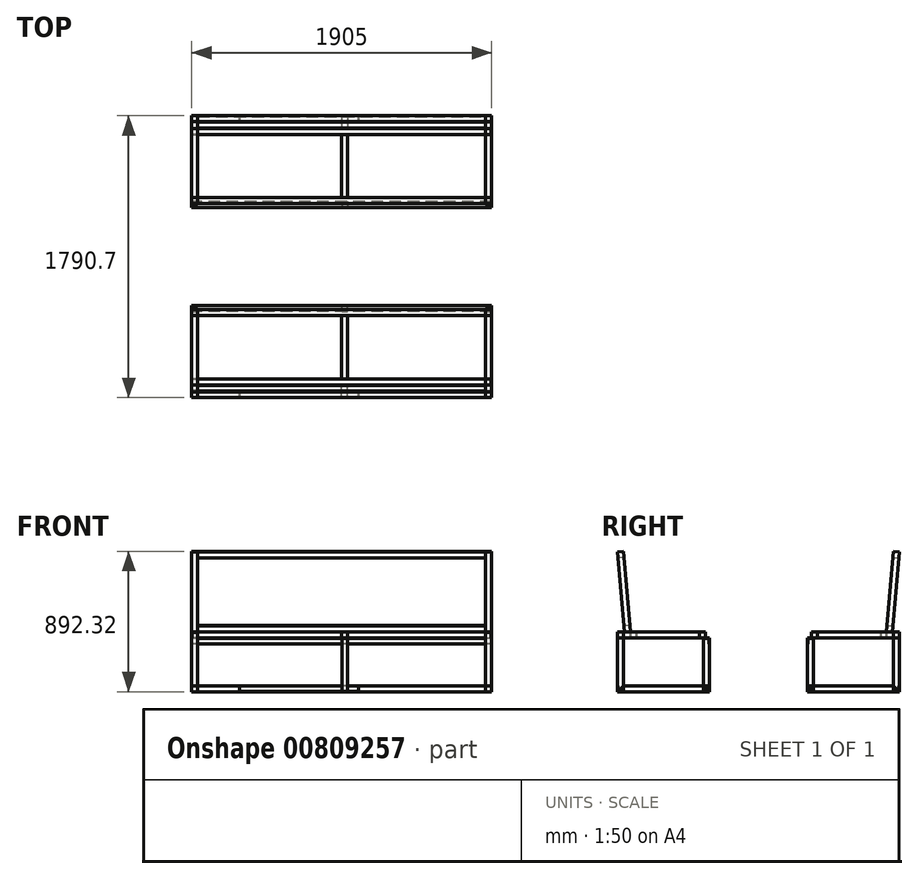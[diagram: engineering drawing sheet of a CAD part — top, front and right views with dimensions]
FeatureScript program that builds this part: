
annotation { "Feature Type Name" : "Feature", "Feature Type Description" : "" }
export const myFeature = defineFeature(function(context is Context, id is Id, definition is map)
    precondition{}
    {
        {
            var Q0;
            Q0=qCreatedBy(makeId("Front.planeOp"),FACE);
            var sketch = newSketch(context, id + "F0", { "sketchPlane" : qUnion([Q0])});
            skLineSegment(sketch, "E0", {"start": v(0, 0) * mm, "end": v(0, 38.1) * mm});
            skLineSegment(sketch, "E1", {"start": v(0, 0) * mm, "end": v(38.1, 0) * mm});
            skLineSegment(sketch, "E2", {"start": v(0, 38.1) * mm, "end": v(3.17, 38.1) * mm});
            skLineSegment(sketch, "E3", {"start": v(3.17, 38.1) * mm, "end": v(3.18, 3.17) * mm});
            skLineSegment(sketch, "E4", {"start": v(3.18, 3.17) * mm, "end": v(38.1, 3.17) * mm});
            skLineSegment(sketch, "E5", {"start": v(38.1, 3.17) * mm, "end": v(38.1, 0) * mm});
            skSolve(sketch);
        }
        {
            var Q0;
            Q0 = qSketchRegion(id + "F0", true);
            extrude(context, id + "F1", {"entities" : qUnion([Q0]), "endBound" : BoundingType.SYMMETRIC, "depth" : 584.2 * mm, "offsetDistance" : 25.4 * mm});
        }
        {
            var Q0;
            Q0=makeQuery(id+"F1.opExtrude","SWEPT_EDGE",EDGE,{"disambiguationData":[OSD([sQuery(id+"F0.wireOp",EDGE,"E2"),sQuery(id+"F0.wireOp",EDGE,"E3")])]});
            var Q1;
            Q1=makeQuery(id+"F1.opExtrude","SWEPT_EDGE",EDGE,{"disambiguationData":[OSD([sQuery(id+"F0.wireOp",EDGE,"E3"),sQuery(id+"F0.wireOp",EDGE,"E4")])]});
            var Q2;
            Q2=makeQuery(id+"F1.opExtrude","SWEPT_EDGE",EDGE,{"disambiguationData":[OSD([sQuery(id+"F0.wireOp",EDGE,"E4"),sQuery(id+"F0.wireOp",EDGE,"E5")])]});
            fillet(context, id + "F2", {"entities" : qUnion([Q0, Q1, Q2]), "radius" : 3.17 * mm, "tangentPropagation" : true, "allowEdgeOverflow" : false});
        }
        {
            var Q0;
            Q0=makeQuery(id+"F1.opExtrude","SWEPT_FACE",FACE,{"disambiguationData":[OSD([sQuery(id+"F0.wireOp",EDGE,"E0")])]});
            var sketch = newSketch(context, id + "F3", { "sketchPlane" : qUnion([Q0])});
            skLineSegment(sketch, "E6", {"start": v(-292.1, 0) * mm, "end": v(-254, 38.1) * mm});
            skSolve(sketch);
        }
        {
            var Q0;
            Q0 = qSketchRegion(id + "F3", true);
            var Q1;
            {var subQ0=sQuery(id+"F3.wireOp",EDGE,"E6");Q1=makeQuery(id+"F3.imprint","IMPRINT",FACE,{"disambiguationData":[TD([[makeQuery(id+"F3.imprint","IMPRINT",EDGE,{"derivedFrom":subQ0}),1.0]])]});}
            extrude(context, id + "F4", {"entities" : qUnion([Q0, Q1]), "operationType" : NewBodyOperationType.REMOVE, "endBound" : BoundingType.THROUGH_ALL, "oppositeDirection" : true, "depth" : 25.4 * mm, "offsetDistance" : 25.4 * mm});
        }
        {
            var Q0;
            Q0=qCreatedBy(makeId("Top.planeOp"),FACE);
            cPlane(context, id + "F5", {"entities" : qUnion([Q0]), "cplaneType" : CPlaneType.OFFSET, "offset" : 190.5 * mm, "width" : 152.4 * mm, "height" : 152.4 * mm});
        }
        {
            var Q0;
            Q0=qCreatedBy(id+"F5.planeOp",FACE);
            var sketch = newSketch(context, id + "F6", { "sketchPlane" : qUnion([Q0])});
            skLineSegment(sketch, "E7", {"start": v(38.1, 292.1) * mm, "end": v(0, 292.1) * mm});
            skLineSegment(sketch, "E8", {"start": v(0, 292.1) * mm, "end": v(0, 254) * mm});
            skLineSegment(sketch, "E9", {"start": v(38.1, 292.1) * mm, "end": v(38.1, 288.93) * mm});
            skLineSegment(sketch, "E10", {"start": v(38.1, 288.93) * mm, "end": v(3.17, 288.93) * mm});
            skLineSegment(sketch, "E11", {"start": v(3.17, 288.93) * mm, "end": v(3.17, 254) * mm});
            skLineSegment(sketch, "E12", {"start": v(3.17, 254) * mm, "end": v(0, 254) * mm});
            skSolve(sketch);
        }
        {
            var Q0;
            Q0 = qSketchRegion(id + "F6", true);
            extrude(context, id + "F7", {"entities" : qUnion([Q0]), "endBound" : BoundingType.SYMMETRIC, "depth" : 381 * mm, "offsetDistance" : 25.4 * mm});
        }
        {
            var Q0;
            Q0=makeQuery(id+"F7.opExtrude","SWEPT_EDGE",EDGE,{"disambiguationData":[OSD([sQuery(id+"F6.wireOp",EDGE,"E9"),sQuery(id+"F6.wireOp",EDGE,"E10")])]});
            var Q1;
            Q1=makeQuery(id+"F7.opExtrude","SWEPT_EDGE",EDGE,{"disambiguationData":[OSD([sQuery(id+"F6.wireOp",EDGE,"E10"),sQuery(id+"F6.wireOp",EDGE,"E11")])]});
            var Q2;
            Q2=makeQuery(id+"F7.opExtrude","SWEPT_EDGE",EDGE,{"disambiguationData":[OSD([sQuery(id+"F6.wireOp",EDGE,"E11"),sQuery(id+"F6.wireOp",EDGE,"E12")])]});
            fillet(context, id + "F8", {"entities" : qUnion([Q0, Q1, Q2]), "radius" : 3.17 * mm, "allowEdgeOverflow" : false});
        }
        {
            var Q0;
            Q0=makeQuery(id+"F7.opExtrude","SWEPT_FACE",FACE,{"disambiguationData":[OSD([sQuery(id+"F6.wireOp",EDGE,"E8")])]});
            var sketch = newSketch(context, id + "F9", { "sketchPlane" : qUnion([Q0])});
            skLineSegment(sketch, "E13", {"start": v(-292.1, 0) * mm, "end": v(-254, 38.1) * mm});
            skLineSegment(sketch, "E14", {"start": v(-254, 38.1) * mm, "end": v(-254, 0) * mm});
            skLineSegment(sketch, "E15", {"start": v(-254, 0) * mm, "end": v(-292.1, 0) * mm});
            skSolve(sketch);
        }
        {
            var Q0;
            Q0 = qSketchRegion(id + "F9", true);
            extrude(context, id + "F10", {"entities" : qUnion([Q0]), "operationType" : NewBodyOperationType.REMOVE, "endBound" : BoundingType.THROUGH_ALL, "oppositeDirection" : true, "depth" : 25.4 * mm, "offsetDistance" : 25.4 * mm});
        }
        {
            var Q0;
            Q0=qCreatedBy(id+"F5.planeOp",FACE);
            var sketch = newSketch(context, id + "F11", { "sketchPlane" : qUnion([Q0])});
            skLineSegment(sketch, "E16", {"start": v(38.1, -292.1) * mm, "end": v(0, -292.1) * mm});
            skLineSegment(sketch, "E17", {"start": v(0, -292.1) * mm, "end": v(0, -254) * mm});
            skLineSegment(sketch, "E18", {"start": v(0, -254) * mm, "end": v(3.18, -254) * mm});
            skLineSegment(sketch, "E19", {"start": v(3.18, -254) * mm, "end": v(3.18, -288.93) * mm});
            skLineSegment(sketch, "E20", {"start": v(3.18, -288.93) * mm, "end": v(38.1, -288.93) * mm});
            skLineSegment(sketch, "E21", {"start": v(38.1, -288.93) * mm, "end": v(38.1, -292.1) * mm});
            skSolve(sketch);
        }
        {
            var Q0;
            Q0 = qSketchRegion(id + "F11", true);
            var Q1;
            Q1=makeQuery(id+"F1.opExtrude","SWEPT_FACE",FACE,{"disambiguationData":[OSD([sQuery(id+"F0.wireOp",EDGE,"E1")])]});
            extrude(context, id + "F12", {"entities" : qUnion([Q0]), "endBound" : BoundingType.UP_TO_SURFACE, "oppositeDirection" : true, "depth" : 25.4 * mm, "endBoundEntityFace" : qUnion([Q1]), "offsetDistance" : 25.4 * mm, "hasSecondDirection" : true, "secondDirectionOppositeDirection" : false, "secondDirectionDepth" : 152.4 * mm});
        }
        {
            var Q0;
            Q0=makeQuery(id+"F12.opExtrude","SWEPT_FACE",FACE,{"disambiguationData":[OSD([sQuery(id+"F11.wireOp",EDGE,"E17")])]});
            var sketch = newSketch(context, id + "F13", { "sketchPlane" : qUnion([Q0])});
            skLineSegment(sketch, "E22", {"start": v(292.1, 342.9) * mm, "end": v(254, 304.8) * mm});
            skLineSegment(sketch, "E23", {"start": v(254, 304.8) * mm, "end": v(254, 342.9) * mm});
            skLineSegment(sketch, "E24", {"start": v(254, 342.9) * mm, "end": v(292.1, 342.9) * mm});
            skSolve(sketch);
        }
        {
            var Q0;
            Q0=makeQuery(id+"F12.opExtrude","SWEPT_FACE",FACE,{"disambiguationData":[OSD([sQuery(id+"F11.wireOp",EDGE,"E17")])]});
            var sketch = newSketch(context, id + "F14", { "sketchPlane" : qUnion([Q0])});
            skLineSegment(sketch, "E25", {"start": v(292.1, 0) * mm, "end": v(254, 38.1) * mm});
            skLineSegment(sketch, "E26", {"start": v(254, 38.1) * mm, "end": v(254, 0) * mm});
            skLineSegment(sketch, "E27", {"start": v(254, 0) * mm, "end": v(292.1, 0) * mm});
            skSolve(sketch);
        }
        {
            var Q0;
            Q0 = qSketchRegion(id + "F14", true);
            extrude(context, id + "F15", {"entities" : qUnion([Q0]), "operationType" : NewBodyOperationType.REMOVE, "endBound" : BoundingType.THROUGH_ALL, "oppositeDirection" : true, "depth" : 25.4 * mm, "offsetDistance" : 25.4 * mm});
        }
        {
            var Q0;
            Q0=makeQuery(id+"F7.opExtrude","SWEPT_FACE",FACE,{"disambiguationData":[OSD([sQuery(id+"F6.wireOp",EDGE,"E7")])]});
            var sketch = newSketch(context, id + "F16", { "sketchPlane" : qUnion([Q0])});
            skLineSegment(sketch, "E28", {"start": v(-38.1, 381) * mm, "end": v(0, 381) * mm});
            skLineSegment(sketch, "E29", {"start": v(0, 381) * mm, "end": v(0, 342.9) * mm});
            skLineSegment(sketch, "E30", {"start": v(-38.1, 381) * mm, "end": v(-38.1, 377.83) * mm});
            skLineSegment(sketch, "E31", {"start": v(-38.1, 377.83) * mm, "end": v(-3.18, 377.83) * mm});
            skLineSegment(sketch, "E32", {"start": v(-3.18, 377.83) * mm, "end": v(-3.18, 342.9) * mm});
            skLineSegment(sketch, "E33", {"start": v(-3.18, 342.9) * mm, "end": v(0, 342.9) * mm});
            skSolve(sketch);
        }
        {
            var Q0;
            Q0 = qSketchRegion(id + "F16", true);
            extrude(context, id + "F17", {"entities" : qUnion([Q0]), "oppositeDirection" : true, "depth" : 558.8 * mm, "offsetDistance" : 25.4 * mm});
        }
        {
            var Q0;
            Q0=makeQuery(id+"F17.opExtrude","SWEPT_FACE",FACE,{"disambiguationData":[OSD([sQuery(id+"F16.wireOp",EDGE,"E29")])]});
            var sketch = newSketch(context, id + "F18", { "sketchPlane" : qUnion([Q0])});
            skLineSegment(sketch, "E34", {"start": v(266.7, 381) * mm, "end": v(228.6, 342.9) * mm});
            skLineSegment(sketch, "E35", {"start": v(228.6, 342.9) * mm, "end": v(266.7, 342.9) * mm});
            skLineSegment(sketch, "E36", {"start": v(266.7, 342.9) * mm, "end": v(266.7, 381) * mm});
            skSolve(sketch);
        }
        {
            var Q0;
            {var subQ0=sQuery(id+"F13.wireOp",EDGE,"E22");Q0=makeQuery(id+"F13.imprint","IMPRINT",FACE,{"disambiguationData":[TD([[makeQuery(id+"F13.imprint","IMPRINT",EDGE,{"derivedFrom":subQ0}),1.0]])]});}
            var sketch = newSketch(context, id + "F19", { "sketchPlane" : qUnion([Q0])});
            skLineSegment(sketch, "E37", {"start": v(254, 0) * mm, "end": v(292.1, 0) * mm});
            skLineSegment(sketch, "E38", {"start": v(292.1, 0) * mm, "end": v(292.1, 38.1) * mm});
            skLineSegment(sketch, "E39", {"start": v(292.1, 38.1) * mm, "end": v(288.93, 38.1) * mm});
            skLineSegment(sketch, "E40", {"start": v(288.93, 38.1) * mm, "end": v(288.93, 3.17) * mm});
            skLineSegment(sketch, "E41", {"start": v(288.93, 3.17) * mm, "end": v(254, 3.17) * mm});
            skLineSegment(sketch, "E42", {"start": v(254, 3.17) * mm, "end": v(254, 0) * mm});
            skSolve(sketch);
        }
        {
            var Q0;
            Q0 = qSketchRegion(id + "F19", true);
            extrude(context, id + "F20", {"entities" : qUnion([Q0]), "oppositeDirection" : true, "depth" : 1905 * mm, "offsetDistance" : 25.4 * mm});
        }
        {
            var Q0;
            {var subQ0=sQuery(id+"F13.wireOp",EDGE,"E22");Q0=makeQuery(id+"F13.imprint","IMPRINT",FACE,{"disambiguationData":[TD([[makeQuery(id+"F13.imprint","IMPRINT",EDGE,{"derivedFrom":subQ0}),1.0]])]});}
            var sketch = newSketch(context, id + "F21", { "sketchPlane" : qUnion([Q0])});
            skLineSegment(sketch, "E43", {"start": v(292.1, 304.8) * mm, "end": v(292.1, 342.9) * mm});
            skLineSegment(sketch, "E44", {"start": v(292.1, 342.9) * mm, "end": v(254, 342.9) * mm});
            skLineSegment(sketch, "E45", {"start": v(254, 342.9) * mm, "end": v(254, 339.73) * mm});
            skLineSegment(sketch, "E46", {"start": v(254, 339.73) * mm, "end": v(288.93, 339.73) * mm});
            skLineSegment(sketch, "E47", {"start": v(288.93, 339.73) * mm, "end": v(288.93, 304.8) * mm});
            skLineSegment(sketch, "E48", {"start": v(288.93, 304.8) * mm, "end": v(292.1, 304.8) * mm});
            skSolve(sketch);
        }
        {
            var Q0;
            Q0 = qSketchRegion(id + "F21", true);
            extrude(context, id + "F22", {"entities" : qUnion([Q0]), "oppositeDirection" : true, "depth" : 1905 * mm, "offsetDistance" : 25.4 * mm});
        }
        {
            var Q0;
            Q0=makeQuery(id+"F18.imprint","IMPRINT",FACE,{"disambiguationData":[TD([[makeQuery(id+"F18.imprint","IMPRINT",EDGE,{"derivedFrom":sQuery(id+"F18.wireOp",EDGE,"E34")}),1.0]])]});
            var sketch = newSketch(context, id + "F23", { "sketchPlane" : qUnion([Q0])});
            skLineSegment(sketch, "E49", {"start": v(228.6, 381) * mm, "end": v(266.7, 381) * mm});
            skLineSegment(sketch, "E50", {"start": v(266.7, 381) * mm, "end": v(266.7, 342.9) * mm});
            skLineSegment(sketch, "E51", {"start": v(266.7, 342.9) * mm, "end": v(228.6, 342.9) * mm});
            skLineSegment(sketch, "E52", {"start": v(228.6, 342.9) * mm, "end": v(228.6, 381) * mm});
            skSolve(sketch);
        }
        {
            var Q0;
            Q0 = qSketchRegion(id + "F23", true);
            extrude(context, id + "F24", {"entities" : qUnion([Q0]), "oppositeDirection" : true, "depth" : 1905 * mm, "offsetDistance" : 25.4 * mm});
        }
        {
            var Q0;
            Q0=makeQuery(id+"F7.opExtrude","SWEPT_FACE",FACE,{"disambiguationData":[OSD([sQuery(id+"F6.wireOp",EDGE,"E8")])]});
            var sketch = newSketch(context, id + "F25", { "sketchPlane" : qUnion([Q0])});
            skLineSegment(sketch, "E53", {"start": v(-292.1, 38.1) * mm, "end": v(-292.1, 0) * mm});
            skLineSegment(sketch, "E54", {"start": v(-292.1, 0) * mm, "end": v(-254, 0) * mm});
            skLineSegment(sketch, "E55", {"start": v(-254, 0) * mm, "end": v(-254, 3.17) * mm});
            skLineSegment(sketch, "E56", {"start": v(-254, 3.17) * mm, "end": v(-288.93, 3.17) * mm});
            skLineSegment(sketch, "E57", {"start": v(-288.93, 3.17) * mm, "end": v(-288.93, 38.1) * mm});
            skLineSegment(sketch, "E58", {"start": v(-288.93, 38.1) * mm, "end": v(-292.1, 38.1) * mm});
            skSolve(sketch);
        }
        {
            var Q0;
            Q0 = qSketchRegion(id + "F25", true);
            extrude(context, id + "F26", {"entities" : qUnion([Q0]), "oppositeDirection" : true, "depth" : 304.8 * mm, "offsetDistance" : 25.4 * mm});
        }
        {
            var Q0;
            Q0=makeQuery(id+"F22.opExtrude","SWEPT_EDGE",EDGE,{"disambiguationData":[OSD([sQuery(id+"F11.wireOp",EDGE,"E16"),sQuery(id+"F11.wireOp",EDGE,"E17"),sQuery(id+"F21.wireOp",EDGE,"E43"),sQuery(id+"F21.wireOp",EDGE,"E48")])]});
            cPoint(context, id + "F27", {"entities" : qUnion([Q0]), "parameter" : 0.5});
        }
        {
            var Q0;
            Q0=makeQuery(id+"F22.opExtrude","SWEPT_EDGE",EDGE,{"disambiguationData":[OSD([sQuery(id+"F13.wireOp",EDGE,"E22"),sQuery(id+"F21.wireOp",EDGE,"E43"),sQuery(id+"F21.wireOp",EDGE,"E44")])]});
            cPoint(context, id + "F28", {"entities" : qUnion([Q0]), "parameter" : 0.5});
        }
        {
            var Q0;
            Q0=makeQuery(id+"F24.opExtrude","SWEPT_EDGE",EDGE,{"disambiguationData":[OSD([sQuery(id+"F18.wireOp",EDGE,"E34"),sQuery(id+"F23.wireOp",EDGE,"E49"),sQuery(id+"F23.wireOp",EDGE,"E50")])]});
            cPoint(context, id + "F29", {"entities" : qUnion([Q0]), "parameter" : 0.5});
        }
        {
            var Q0;
            Q0 = qCreatedBy(id + "F27" ,VERTEX);
            var Q1;
            Q1 = qCreatedBy(id + "F28" ,VERTEX);
            var Q2;
            Q2 = qCreatedBy(id + "F29" ,VERTEX);
            cPlane(context, id + "F30", {"entities" : qUnion([Q0, Q1, Q2]), "cplaneType" : CPlaneType.THREE_POINT, "offset" : 25.4 * mm, "width" : 152.4 * mm, "height" : 152.4 * mm});
        }
        {
            var Q0;
            Q0=makeQuery(id+"F17.opExtrude","SWEPT_BODY",BODY,{"disambiguationData":[OSD([sQuery(id+"F16.wireOp",EDGE,"E28"),sQuery(id+"F16.wireOp",EDGE,"E29"),sQuery(id+"F16.wireOp",EDGE,"E30"),sQuery(id+"F16.wireOp",EDGE,"E31"),sQuery(id+"F16.wireOp",EDGE,"E32"),sQuery(id+"F16.wireOp",EDGE,"E33")])]});
            var Q1;
            Q1=makeQuery(id+"F7.opExtrude","SWEPT_BODY",BODY,{"disambiguationData":[OSD([sQuery(id+"F6.wireOp",EDGE,"E7"),sQuery(id+"F6.wireOp",EDGE,"E8"),sQuery(id+"F6.wireOp",EDGE,"E9"),sQuery(id+"F6.wireOp",EDGE,"E10"),sQuery(id+"F6.wireOp",EDGE,"E11"),sQuery(id+"F6.wireOp",EDGE,"E12")])]});
            var Q2;
            Q2=makeQuery(id+"F12.opExtrude","SWEPT_BODY",BODY,{"disambiguationData":[OSD([sQuery(id+"F11.wireOp",EDGE,"E16"),sQuery(id+"F11.wireOp",EDGE,"E17"),sQuery(id+"F11.wireOp",EDGE,"E18"),sQuery(id+"F11.wireOp",EDGE,"E19"),sQuery(id+"F11.wireOp",EDGE,"E20"),sQuery(id+"F11.wireOp",EDGE,"E21")])]});
            var Q3;
            Q3=makeQuery(id+"F1.opExtrude","SWEPT_BODY",BODY,{"disambiguationData":[OSD([sQuery(id+"F0.wireOp",EDGE,"E0"),sQuery(id+"F0.wireOp",EDGE,"E1"),sQuery(id+"F0.wireOp",EDGE,"E2"),sQuery(id+"F0.wireOp",EDGE,"E3"),sQuery(id+"F0.wireOp",EDGE,"E4"),sQuery(id+"F0.wireOp",EDGE,"E5")])]});
            var Q4;
            Q4=qCreatedBy(id+"F30.planeOp",FACE);
            mirror(context, id + "F31", {"entities" : qUnion([Q0, Q1, Q2, Q3]), "mirrorPlane" : qUnion([Q4])});
        }
        {
            var Q0;
            Q0=makeQuery(id+"F31.opPattern","COPY",FACE,{"derivedFrom":makeQuery(id+"F1.opExtrude","SWEPT_FACE",FACE,{"disambiguationData":[OSD([sQuery(id+"F0.wireOp",EDGE,"E0")])]}),"instanceName":"1"});
            var sketch = newSketch(context, id + "F32", { "sketchPlane" : qUnion([Q0])});
            skLineSegment(sketch, "E59", {"start": v(292.1, 38.1) * mm, "end": v(292.1, 0) * mm});
            skLineSegment(sketch, "E60", {"start": v(292.1, 0) * mm, "end": v(254, 0) * mm});
            skLineSegment(sketch, "E61", {"start": v(254, 0) * mm, "end": v(254, 3.17) * mm});
            skLineSegment(sketch, "E62", {"start": v(254, 3.17) * mm, "end": v(288.93, 3.17) * mm});
            skLineSegment(sketch, "E63", {"start": v(288.93, 3.17) * mm, "end": v(288.93, 38.1) * mm});
            skLineSegment(sketch, "E64", {"start": v(288.93, 38.1) * mm, "end": v(292.1, 38.1) * mm});
            skSolve(sketch);
        }
        {
            var Q0;
            Q0 = qSketchRegion(id + "F32", true);
            extrude(context, id + "F33", {"entities" : qUnion([Q0]), "oppositeDirection" : true, "depth" : 845.82 * mm, "offsetDistance" : 25.4 * mm});
        }
        {
            var Q0;
            {var subQ0=sQuery(id+"F18.wireOp",EDGE,"E34");Q0=makeQuery(id+"F18.imprint","IMPRINT",FACE,{"disambiguationData":[TD([[makeQuery(id+"F18.imprint","IMPRINT",EDGE,{"derivedFrom":subQ0}),-1.0]])]});}
            var sketch = newSketch(context, id + "F34", { "sketchPlane" : qUnion([Q0])});
            skLineSegment(sketch, "E65", {"start": v(-247.66, 381) * mm, "end": v(-292.1, 889) * mm});
            skLineSegment(sketch, "E66", {"start": v(-247.66, 381) * mm, "end": v(-209.7, 384.32) * mm});
            skLineSegment(sketch, "E67", {"start": v(-209.7, 384.32) * mm, "end": v(-254.14, 892.32) * mm});
            skLineSegment(sketch, "E68", {"start": v(-254.14, 892.32) * mm, "end": v(-292.1, 889) * mm});
            skSolve(sketch);
        }
        {
            var Q0;
            Q0 = qSketchRegion(id + "F34", true);
            extrude(context, id + "F35", {"entities" : qUnion([Q0]), "oppositeDirection" : true, "depth" : 38.1 * mm, "offsetDistance" : 25.4 * mm});
        }
        {
            var Q0;
            Q0=makeQuery(id+"F35.opExtrude","SWEPT_BODY",BODY,{"disambiguationData":[OSD([sQuery(id+"F34.wireOp",EDGE,"E65"),sQuery(id+"F34.wireOp",EDGE,"E66"),sQuery(id+"F34.wireOp",EDGE,"E67"),sQuery(id+"F34.wireOp",EDGE,"E68")])]});
            var Q1;
            Q1=qCreatedBy(id+"F30.planeOp",FACE);
            mirror(context, id + "F36", {"entities" : qUnion([Q0]), "mirrorPlane" : qUnion([Q1])});
        }
        {
            var Q0;
            Q0=makeQuery(id+"F36.opPattern","COPY",FACE,{"derivedFrom":makeQuery(id+"F35.opExtrude","CAP_FACE",FACE,{"disambiguationData":[OSD([sQuery(id+"F34.wireOp",EDGE,"E65"),sQuery(id+"F34.wireOp",EDGE,"E66"),sQuery(id+"F34.wireOp",EDGE,"E67"),sQuery(id+"F34.wireOp",EDGE,"E68")])],"isStart":false}),"instanceName":"1"});
            var sketch = newSketch(context, id + "F37", { "sketchPlane" : qUnion([Q0])});
            skLineSegment(sketch, "E69", {"start": v(-247.66, 381) * mm, "end": v(-209.7, 384.32) * mm});
            skLineSegment(sketch, "E70", {"start": v(-209.7, 384.32) * mm, "end": v(-213.02, 422.28) * mm});
            skLineSegment(sketch, "E71", {"start": v(-213.02, 422.28) * mm, "end": v(-250.98, 418.96) * mm});
            skLineSegment(sketch, "E72", {"start": v(-250.98, 418.96) * mm, "end": v(-247.66, 381) * mm});
            skSolve(sketch);
        }
        {
            var Q0;
            Q0 = qSketchRegion(id + "F37", true);
            extrude(context, id + "F38", {"entities" : qUnion([Q0]), "endBound" : BoundingType.UP_TO_NEXT, "depth" : 25.4 * mm, "offsetDistance" : 25.4 * mm});
        }
        {
            var Q0;
            Q0=makeQuery(id+"F36.opPattern","COPY",FACE,{"derivedFrom":makeQuery(id+"F35.opExtrude","CAP_FACE",FACE,{"disambiguationData":[OSD([sQuery(id+"F34.wireOp",EDGE,"E65"),sQuery(id+"F34.wireOp",EDGE,"E66"),sQuery(id+"F34.wireOp",EDGE,"E67"),sQuery(id+"F34.wireOp",EDGE,"E68")])],"isStart":false}),"instanceName":"1"});
            var sketch = newSketch(context, id + "F39", { "sketchPlane" : qUnion([Q0])});
            skLineSegment(sketch, "E73", {"start": v(-292.1, 889) * mm, "end": v(-254.14, 892.32) * mm});
            skLineSegment(sketch, "E74", {"start": v(-254.14, 892.32) * mm, "end": v(-250.82, 854.37) * mm});
            skLineSegment(sketch, "E75", {"start": v(-250.82, 854.37) * mm, "end": v(-288.78, 851.04) * mm});
            skLineSegment(sketch, "E76", {"start": v(-288.78, 851.04) * mm, "end": v(-292.1, 889) * mm});
            skSolve(sketch);
        }
        {
            var Q0;
            Q0 = qSketchRegion(id + "F39", true);
            extrude(context, id + "F40", {"entities" : qUnion([Q0]), "endBound" : BoundingType.UP_TO_NEXT, "depth" : 25.4 * mm, "offsetDistance" : 25.4 * mm});
        }
        {
            var Q0;
            Q0=makeQuery(id+"F31.opPattern","COPY",FACE,{"derivedFrom":makeQuery(id+"F17.opExtrude","SWEPT_FACE",FACE,{"disambiguationData":[OSD([sQuery(id+"F16.wireOp",EDGE,"E32")])]}),"instanceName":"1"});
            var sketch = newSketch(context, id + "F41", { "sketchPlane" : qUnion([Q0])});
            skLineSegment(sketch, "E77.bottom", {"start": v(-171.6, 342.9) * mm, "end": v(-209.7, 342.9) * mm});
            skLineSegment(sketch, "E77.top", {"start": v(-171.6, 381) * mm, "end": v(-209.7, 381) * mm});
            skLineSegment(sketch, "E77.left", {"start": v(-171.6, 342.9) * mm, "end": v(-171.6, 381) * mm});
            skLineSegment(sketch, "E77.right", {"start": v(-209.7, 342.9) * mm, "end": v(-209.7, 381) * mm});
            skSolve(sketch);
        }
        {
            var Q0;
            Q0 = qSketchRegion(id + "F41", true);
            extrude(context, id + "F42", {"entities" : qUnion([Q0]), "endBound" : BoundingType.UP_TO_NEXT, "depth" : 25.4 * mm, "offsetDistance" : 25.4 * mm});
        }
        {
            var Q0;
            Q0=makeQuery(id+"F20.opExtrude","SWEPT_FACE",FACE,{"disambiguationData":[OSD([sQuery(id+"F19.wireOp",EDGE,"E38")])]});
            cPlane(context, id + "F43", {"entities" : qUnion([Q0]), "cplaneType" : CPlaneType.OFFSET, "offset" : 311.15 * mm, "width" : 152.4 * mm, "height" : 152.4 * mm});
        }
        {
            var Q0;
            Q0=makeQuery(id+"F42.opExtrude","SWEPT_FACE",FACE,{"disambiguationData":[OSD([sQuery(id+"F41.wireOp",EDGE,"E77.left")])]});
            var sketch = newSketch(context, id + "F44", { "sketchPlane" : qUnion([Q0])});
            skLineSegment(sketch, "E78.bottom", {"start": v(950.91, 381) * mm, "end": v(989.01, 381) * mm});
            skLineSegment(sketch, "E78.top", {"start": v(950.91, 342.9) * mm, "end": v(989.01, 342.9) * mm});
            skLineSegment(sketch, "E78.left", {"start": v(950.91, 381) * mm, "end": v(950.91, 342.9) * mm});
            skLineSegment(sketch, "E78.right", {"start": v(989.01, 381) * mm, "end": v(989.01, 342.9) * mm});
            skPoint(sketch, "E79", {"position": v(969.96, 381) * mm});
            skSolve(sketch);
        }
        {
            var Q0;
            Q0 = qSketchRegion(id + "F44", true);
            extrude(context, id + "F45", {"entities" : qUnion([Q0]), "endBound" : BoundingType.UP_TO_NEXT, "depth" : 25.4 * mm, "offsetDistance" : 25.4 * mm});
        }
        {
            var Q0;
            Q0=makeQuery(id+"F17.opExtrude","SWEPT_FACE",FACE,{"disambiguationData":[OSD([sQuery(id+"F16.wireOp",EDGE,"E28")])]});
            var sketch = newSketch(context, id + "F46", { "sketchPlane" : qUnion([Q0])});
            skLineSegment(sketch, "E80.bottom", {"start": v(0, 190.65) * mm, "end": v(1905, 190.65) * mm});
            skLineSegment(sketch, "E80.top", {"start": v(0, -266.7) * mm, "end": v(1905, -266.7) * mm});
            skLineSegment(sketch, "E80.left", {"start": v(0, 190.65) * mm, "end": v(0, -266.7) * mm});
            skLineSegment(sketch, "E80.right", {"start": v(1905, 190.65) * mm, "end": v(1905, -266.7) * mm});
            skSolve(sketch);
        }
        {
            var Q0;
            Q0=makeQuery(id+"F40.opExtrude","SWEPT_FACE",FACE,{"disambiguationData":[OSD([sQuery(id+"F39.wireOp",EDGE,"E74")])]});
            var sketch = newSketch(context, id + "F47", { "sketchPlane" : qUnion([Q0])});
            skLineSegment(sketch, "E81", {"start": v(38.1, 872.98) * mm, "end": v(1866.9, 872.98) * mm});
            skLineSegment(sketch, "E82", {"start": v(1866.9, 872.98) * mm, "end": v(1866.9, 439.23) * mm});
            skLineSegment(sketch, "E83", {"start": v(1866.9, 439.23) * mm, "end": v(38.1, 439.23) * mm});
            skLineSegment(sketch, "E84", {"start": v(38.1, 439.23) * mm, "end": v(38.1, 872.98) * mm});
            skSolve(sketch);
        }
        {
            var Q0;
            Q0=makeQuery(id+"F20.opExtrude","SWEPT_FACE",FACE,{"disambiguationData":[OSD([sQuery(id+"F19.wireOp",EDGE,"E41")])]});
            var sketch = newSketch(context, id + "F48", { "sketchPlane" : qUnion([Q0])});
            skLineSegment(sketch, "E85.bottom", {"start": v(989.01, -288.93) * mm, "end": v(954.09, -288.93) * mm});
            skLineSegment(sketch, "E85.top", {"start": v(989.01, -254) * mm, "end": v(954.09, -254) * mm});
            skLineSegment(sketch, "E85.left", {"start": v(989.01, -288.93) * mm, "end": v(989.01, -254) * mm});
            skLineSegment(sketch, "E85.right", {"start": v(954.09, -288.93) * mm, "end": v(954.09, -254) * mm});
            skSolve(sketch);
        }
        {
            var Q0;
            Q0 = qSketchRegion(id + "F48", true);
            extrude(context, id + "F49", {"entities" : qUnion([Q0]), "endBound" : BoundingType.UP_TO_NEXT, "depth" : 25.4 * mm, "offsetDistance" : 25.4 * mm});
        }
        {
            var Q0;
            Q0=makeQuery(id+"F42.opExtrude","SWEPT_FACE",FACE,{"disambiguationData":[OSD([sQuery(id+"F41.wireOp",EDGE,"E77.right")])]});
            var sketch = newSketch(context, id + "F50", { "sketchPlane" : qUnion([Q0])});
            skLineSegment(sketch, "E86.bottom", {"start": v(-989.01, 381) * mm, "end": v(-950.91, 381) * mm});
            skLineSegment(sketch, "E86.top", {"start": v(-989.01, 342.9) * mm, "end": v(-950.91, 342.9) * mm});
            skLineSegment(sketch, "E86.left", {"start": v(-989.01, 381) * mm, "end": v(-989.01, 342.9) * mm});
            skLineSegment(sketch, "E86.right", {"start": v(-950.91, 381) * mm, "end": v(-950.91, 342.9) * mm});
            skSolve(sketch);
        }
        {
            var Q0;
            Q0 = qSketchRegion(id + "F50", true);
            var Q1;
            Q1=makeQuery(id+"F31.opPattern","COPY",FACE,{"derivedFrom":makeQuery(id+"F7.opExtrude","SWEPT_FACE",FACE,{"disambiguationData":[OSD([sQuery(id+"F6.wireOp",EDGE,"E7")])]}),"instanceName":"1"});
            extrude(context, id + "F51", {"entities" : qUnion([Q0]), "endBound" : BoundingType.UP_TO_SURFACE, "depth" : 25.4 * mm, "endBoundEntityFace" : qUnion([Q1]), "offsetDistance" : 25.4 * mm});
        }
        {
            var Q0;
            Q0=makeQuery(id+"F1.opExtrude","SWEPT_BODY",BODY,{"disambiguationData":[OSD([sQuery(id+"F0.wireOp",EDGE,"E0"),sQuery(id+"F0.wireOp",EDGE,"E1"),sQuery(id+"F0.wireOp",EDGE,"E2"),sQuery(id+"F0.wireOp",EDGE,"E3"),sQuery(id+"F0.wireOp",EDGE,"E4"),sQuery(id+"F0.wireOp",EDGE,"E5")])]});
            var Q1;
            Q1=makeQuery(id+"F7.opExtrude","SWEPT_BODY",BODY,{"disambiguationData":[OSD([sQuery(id+"F6.wireOp",EDGE,"E7"),sQuery(id+"F6.wireOp",EDGE,"E8"),sQuery(id+"F6.wireOp",EDGE,"E9"),sQuery(id+"F6.wireOp",EDGE,"E10"),sQuery(id+"F6.wireOp",EDGE,"E11"),sQuery(id+"F6.wireOp",EDGE,"E12")])]});
            var Q2;
            Q2=makeQuery(id+"F12.opExtrude","SWEPT_BODY",BODY,{"disambiguationData":[OSD([sQuery(id+"F11.wireOp",EDGE,"E16"),sQuery(id+"F11.wireOp",EDGE,"E17"),sQuery(id+"F11.wireOp",EDGE,"E18"),sQuery(id+"F11.wireOp",EDGE,"E19"),sQuery(id+"F11.wireOp",EDGE,"E20"),sQuery(id+"F11.wireOp",EDGE,"E21")])]});
            var Q3;
            Q3=makeQuery(id+"F17.opExtrude","SWEPT_BODY",BODY,{"disambiguationData":[OSD([sQuery(id+"F16.wireOp",EDGE,"E28"),sQuery(id+"F16.wireOp",EDGE,"E29"),sQuery(id+"F16.wireOp",EDGE,"E30"),sQuery(id+"F16.wireOp",EDGE,"E31"),sQuery(id+"F16.wireOp",EDGE,"E32"),sQuery(id+"F16.wireOp",EDGE,"E33")])]});
            var Q4;
            Q4=makeQuery(id+"F20.opExtrude","SWEPT_BODY",BODY,{"disambiguationData":[OSD([sQuery(id+"F19.wireOp",EDGE,"E37"),sQuery(id+"F19.wireOp",EDGE,"E38"),sQuery(id+"F19.wireOp",EDGE,"E39"),sQuery(id+"F19.wireOp",EDGE,"E40"),sQuery(id+"F19.wireOp",EDGE,"E41"),sQuery(id+"F19.wireOp",EDGE,"E42")])]});
            var Q5;
            Q5=makeQuery(id+"F22.opExtrude","SWEPT_BODY",BODY,{"disambiguationData":[OSD([sQuery(id+"F21.wireOp",EDGE,"E43"),sQuery(id+"F21.wireOp",EDGE,"E44"),sQuery(id+"F21.wireOp",EDGE,"E45"),sQuery(id+"F21.wireOp",EDGE,"E46"),sQuery(id+"F21.wireOp",EDGE,"E47"),sQuery(id+"F21.wireOp",EDGE,"E48")])]});
            var Q6;
            Q6=makeQuery(id+"F24.opExtrude","SWEPT_BODY",BODY,{"disambiguationData":[OSD([sQuery(id+"F23.wireOp",EDGE,"E49"),sQuery(id+"F23.wireOp",EDGE,"E50"),sQuery(id+"F23.wireOp",EDGE,"E51"),sQuery(id+"F23.wireOp",EDGE,"8kfbenor-xNS7-9wQ0-rUgi-srJCy245hN0V"),sQuery(id+"F23.wireOp",EDGE,"DvwX7SPe-Yicc-RiZt-PwwJ-qJhFAhnkWR2l"),sQuery(id+"F23.wireOp",EDGE,"E52")])]});
            var Q7;
            Q7=makeQuery(id+"F26.opExtrude","SWEPT_BODY",BODY,{"disambiguationData":[OSD([sQuery(id+"F25.wireOp",EDGE,"E53"),sQuery(id+"F25.wireOp",EDGE,"E54"),sQuery(id+"F25.wireOp",EDGE,"E55"),sQuery(id+"F25.wireOp",EDGE,"E56"),sQuery(id+"F25.wireOp",EDGE,"E57"),sQuery(id+"F25.wireOp",EDGE,"E58")])]});
            var Q8;
            Q8=makeQuery(id+"F31.opPattern","COPY",BODY,{"derivedFrom":makeQuery(id+"F1.opExtrude","SWEPT_BODY",BODY,{"disambiguationData":[OSD([sQuery(id+"F0.wireOp",EDGE,"E0"),sQuery(id+"F0.wireOp",EDGE,"E1"),sQuery(id+"F0.wireOp",EDGE,"E2"),sQuery(id+"F0.wireOp",EDGE,"E3"),sQuery(id+"F0.wireOp",EDGE,"E4"),sQuery(id+"F0.wireOp",EDGE,"E5")])]}),"instanceName":"1"});
            var Q9;
            Q9=makeQuery(id+"F31.opPattern","COPY",BODY,{"derivedFrom":makeQuery(id+"F7.opExtrude","SWEPT_BODY",BODY,{"disambiguationData":[OSD([sQuery(id+"F6.wireOp",EDGE,"E7"),sQuery(id+"F6.wireOp",EDGE,"E8"),sQuery(id+"F6.wireOp",EDGE,"E9"),sQuery(id+"F6.wireOp",EDGE,"E10"),sQuery(id+"F6.wireOp",EDGE,"E11"),sQuery(id+"F6.wireOp",EDGE,"E12")])]}),"instanceName":"1"});
            var Q10;
            Q10=makeQuery(id+"F31.opPattern","COPY",BODY,{"derivedFrom":makeQuery(id+"F12.opExtrude","SWEPT_BODY",BODY,{"disambiguationData":[OSD([sQuery(id+"F11.wireOp",EDGE,"E16"),sQuery(id+"F11.wireOp",EDGE,"E17"),sQuery(id+"F11.wireOp",EDGE,"E18"),sQuery(id+"F11.wireOp",EDGE,"E19"),sQuery(id+"F11.wireOp",EDGE,"E20"),sQuery(id+"F11.wireOp",EDGE,"E21")])]}),"instanceName":"1"});
            var Q11;
            Q11=makeQuery(id+"F31.opPattern","COPY",BODY,{"derivedFrom":makeQuery(id+"F17.opExtrude","SWEPT_BODY",BODY,{"disambiguationData":[OSD([sQuery(id+"F16.wireOp",EDGE,"E28"),sQuery(id+"F16.wireOp",EDGE,"E29"),sQuery(id+"F16.wireOp",EDGE,"E30"),sQuery(id+"F16.wireOp",EDGE,"E31"),sQuery(id+"F16.wireOp",EDGE,"E32"),sQuery(id+"F16.wireOp",EDGE,"E33")])]}),"instanceName":"1"});
            var Q12;
            Q12=makeQuery(id+"F33.opExtrude","SWEPT_BODY",BODY,{"disambiguationData":[OSD([sQuery(id+"F32.wireOp",EDGE,"E59"),sQuery(id+"F32.wireOp",EDGE,"E60"),sQuery(id+"F32.wireOp",EDGE,"E61"),sQuery(id+"F32.wireOp",EDGE,"E62"),sQuery(id+"F32.wireOp",EDGE,"E63"),sQuery(id+"F32.wireOp",EDGE,"E64")])]});
            var Q13;
            Q13=makeQuery(id+"F35.opExtrude","SWEPT_BODY",BODY,{"disambiguationData":[OSD([sQuery(id+"F34.wireOp",EDGE,"E65"),sQuery(id+"F34.wireOp",EDGE,"E66"),sQuery(id+"F34.wireOp",EDGE,"E67"),sQuery(id+"F34.wireOp",EDGE,"E68")])]});
            var Q14;
            Q14=makeQuery(id+"F36.opPattern","COPY",BODY,{"derivedFrom":makeQuery(id+"F35.opExtrude","SWEPT_BODY",BODY,{"disambiguationData":[OSD([sQuery(id+"F34.wireOp",EDGE,"E65"),sQuery(id+"F34.wireOp",EDGE,"E66"),sQuery(id+"F34.wireOp",EDGE,"E67"),sQuery(id+"F34.wireOp",EDGE,"E68")])]}),"instanceName":"1"});
            var Q15;
            Q15=makeQuery(id+"F38.opExtrude","SWEPT_BODY",BODY,{"disambiguationData":[OSD([sQuery(id+"F37.wireOp",EDGE,"E69"),sQuery(id+"F37.wireOp",EDGE,"E70"),sQuery(id+"F37.wireOp",EDGE,"E71"),sQuery(id+"F37.wireOp",EDGE,"E72")])]});
            var Q16;
            Q16=makeQuery(id+"F40.opExtrude","SWEPT_BODY",BODY,{"disambiguationData":[OSD([sQuery(id+"F39.wireOp",EDGE,"E73"),sQuery(id+"F39.wireOp",EDGE,"E74"),sQuery(id+"F39.wireOp",EDGE,"E75"),sQuery(id+"F39.wireOp",EDGE,"E76")])]});
            var Q17;
            Q17=makeQuery(id+"F42.opExtrude","SWEPT_BODY",BODY,{"disambiguationData":[OSD([sQuery(id+"F41.wireOp",EDGE,"E77.bottom"),sQuery(id+"F41.wireOp",EDGE,"E77.top"),sQuery(id+"F41.wireOp",EDGE,"E77.left"),sQuery(id+"F41.wireOp",EDGE,"E77.right")])]});
            var Q18;
            Q18=makeQuery(id+"F45.opExtrude","SWEPT_BODY",BODY,{"disambiguationData":[OSD([sQuery(id+"F44.wireOp",EDGE,"E78.bottom"),sQuery(id+"F44.wireOp",EDGE,"E78.top"),sQuery(id+"F44.wireOp",EDGE,"E78.left"),sQuery(id+"F44.wireOp",EDGE,"E78.right")])]});
            var Q19;
            Q19=makeQuery(id+"F51.opExtrude","SWEPT_BODY",BODY,{"disambiguationData":[OSD([sQuery(id+"F50.wireOp",EDGE,"E86.bottom"),sQuery(id+"F50.wireOp",EDGE,"E86.top"),sQuery(id+"F50.wireOp",EDGE,"E86.left"),sQuery(id+"F50.wireOp",EDGE,"E86.right")])]});
            var Q20;
            Q20=makeQuery(id+"F49.opExtrude","SWEPT_BODY",BODY,{"disambiguationData":[OSD([sQuery(id+"F48.wireOp",EDGE,"E85.bottom"),sQuery(id+"F48.wireOp",EDGE,"E85.top"),sQuery(id+"F48.wireOp",EDGE,"E85.left"),sQuery(id+"F48.wireOp",EDGE,"E85.right")])]});
            var Q21;
            Q21=qCreatedBy(id+"F43.planeOp",FACE);
            mirror(context, id + "F52", {"entities" : qUnion([Q0, Q1, Q2, Q3, Q4, Q5, Q6, Q7, Q8, Q9, Q10, Q11, Q12, Q13, Q14, Q15, Q16, Q17, Q18, Q19, Q20]), "mirrorPlane" : qUnion([Q21])});
        }
    });
